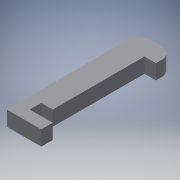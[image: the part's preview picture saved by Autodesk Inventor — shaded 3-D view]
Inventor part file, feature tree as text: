
AUTODESK INVENTOR PART (.ipt)
format: ipt  version: 2017 (Build 210142000, 142)  size: 104,960 bytes
history: native  units: mm
features: extrude x1, sketch x1
ambient origin geometry x8: Origin, YZ Plane, XZ Plane, XY Plane, X Axis, Y Axis, Z Axis, Center Point
bodies: Solid1 (feature_tree)
feature tree (2):
  extrude  "Extrusion1"  Depth=5.0mm
  sketch  "Sketch1"  dims[d0=5.0mm d1=5.0mm d2=5.0mm d3=40.0mm d4=5.0mm d5=7.5mm d6=6.5mm d7=0.0mm d8=10.0mm d9=5.0mm d10=5.0mm]
